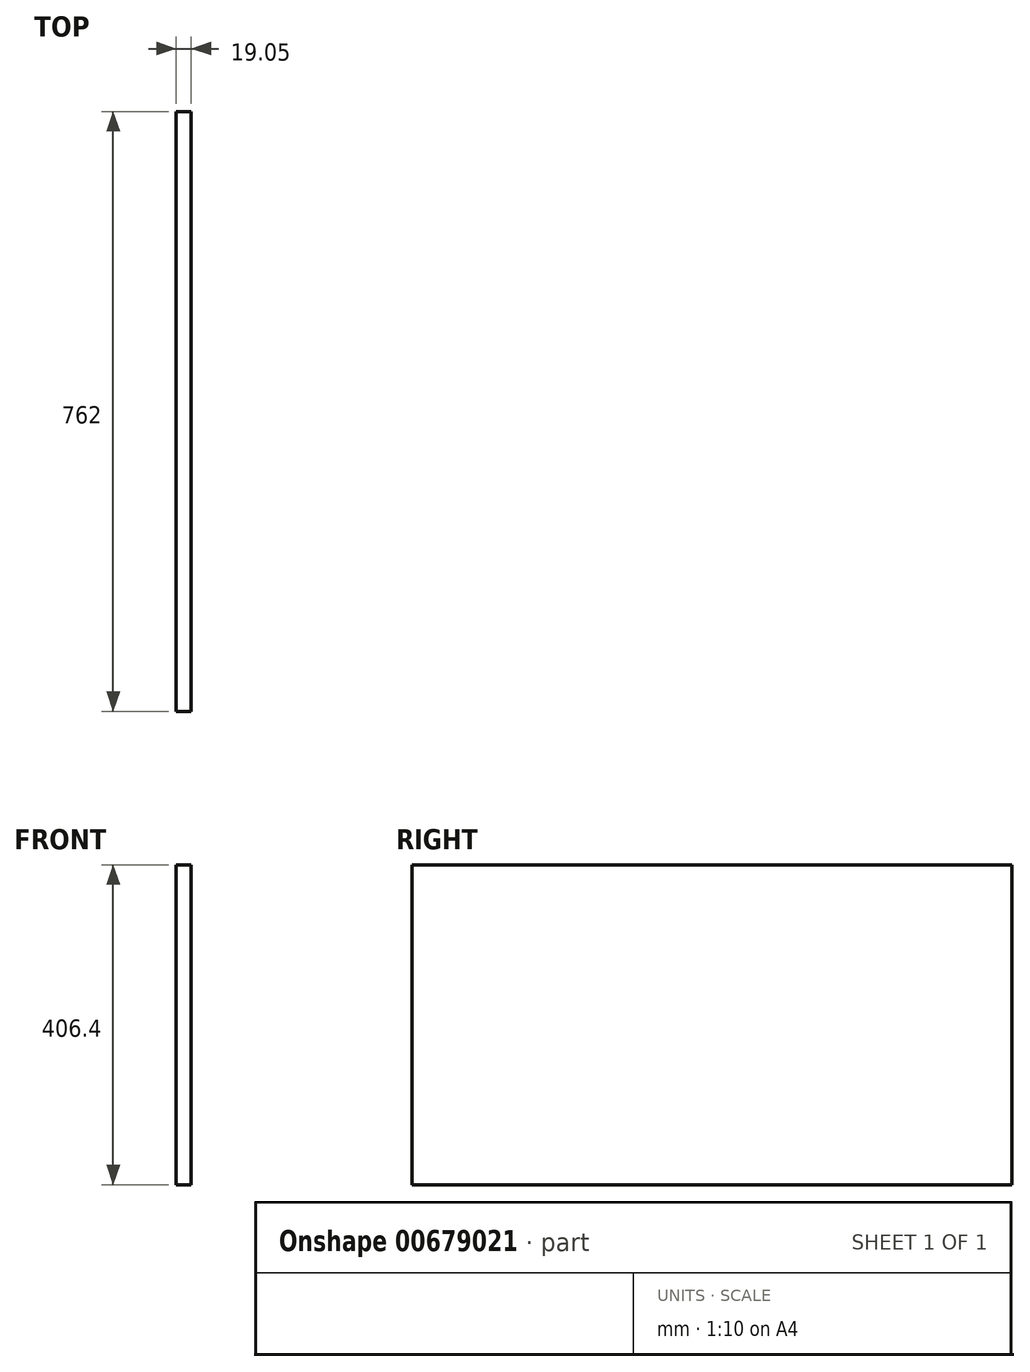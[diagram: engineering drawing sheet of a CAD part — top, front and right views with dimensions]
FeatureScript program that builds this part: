
annotation { "Feature Type Name" : "Feature", "Feature Type Description" : "" }
export const myFeature = defineFeature(function(context is Context, id is Id, definition is map)
    precondition{}
    {
        {
            var Q0;
            Q0=qCreatedBy(makeId("Right.planeOp"),FACE);
            var sketch = newSketch(context, id + "F0", { "sketchPlane" : qUnion([Q0])});
            skLineSegment(sketch, "E0.bottom", {"start": v(381, 203.2) * mm, "end": v(-381, 203.2) * mm});
            skLineSegment(sketch, "E0.top", {"start": v(381, -203.2) * mm, "end": v(-381, -203.2) * mm});
            skLineSegment(sketch, "E0.left", {"start": v(381, 203.2) * mm, "end": v(381, -203.2) * mm});
            skLineSegment(sketch, "E0.right", {"start": v(-381, 203.2) * mm, "end": v(-381, -203.2) * mm});
            skPoint(sketch, "E0.middle", {"position": v(0, 0) * mm});
            skSolve(sketch);
        }
        {
            var Q0;
            Q0=makeQuery(id+"F0.imprint","IMPRINT",FACE,{"disambiguationData":[TD([[makeQuery(id+"F0.imprint","IMPRINT",EDGE,{"derivedFrom":sQuery(id+"F0.wireOp",EDGE,"E0.bottom")}),1.0]])]});
            extrude(context, id + "F1", {"entities" : qUnion([Q0]), "depth" : 19.05 * mm, "offsetDistance" : 25.4 * mm});
        }
    });
